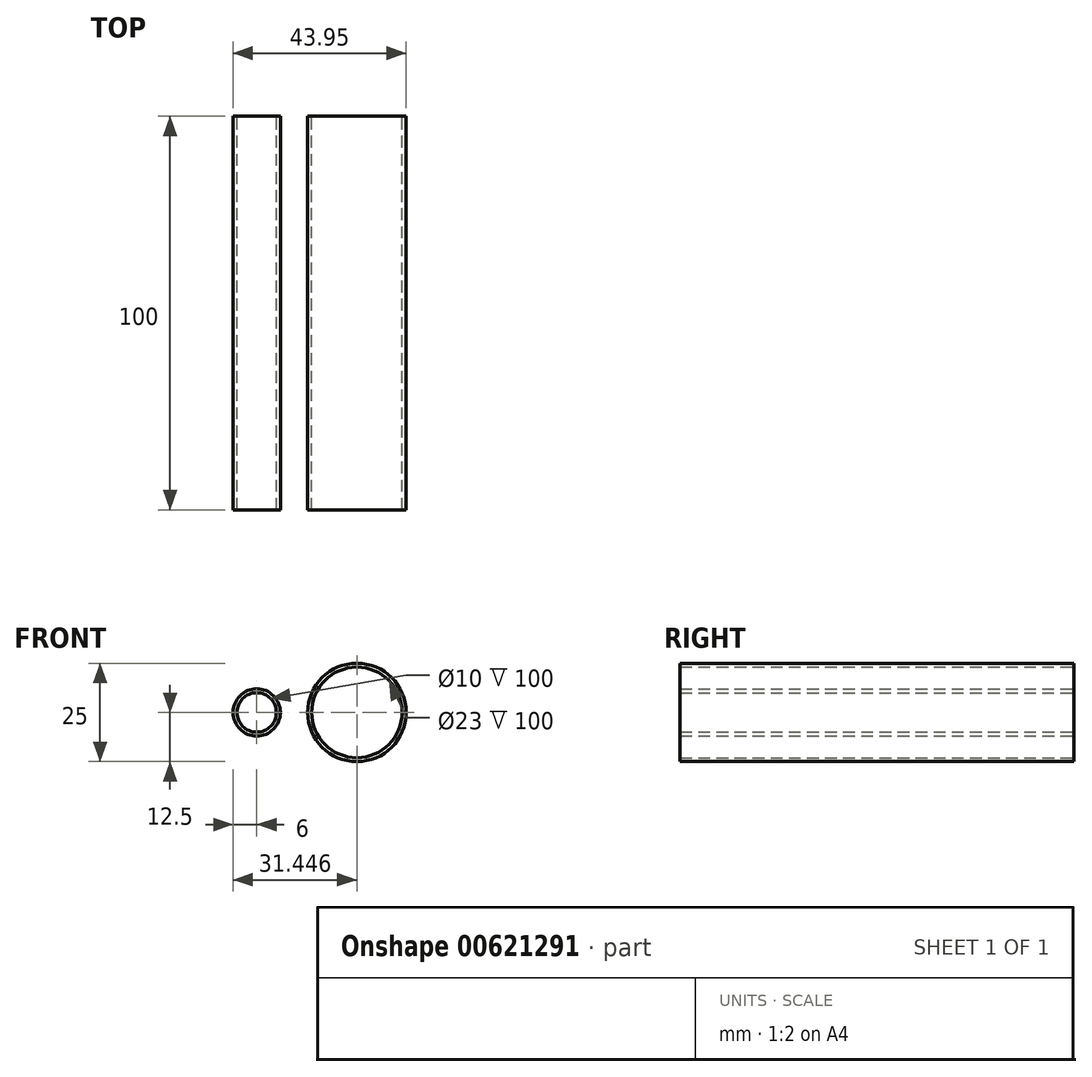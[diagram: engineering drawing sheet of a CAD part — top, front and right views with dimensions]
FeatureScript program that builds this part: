
annotation { "Feature Type Name" : "Feature", "Feature Type Description" : "" }
export const myFeature = defineFeature(function(context is Context, id is Id, definition is map)
    precondition{}
    {
        {
            var Q0;
            Q0=qCreatedBy(makeId("Front.planeOp"),FACE);
            var sketch = newSketch(context, id + "F0", { "sketchPlane" : qUnion([Q0])});
            skCircle(sketch, "E0", {"center": v(0, 0) * mm, "radius": 6 * mm});
            skCircle(sketch, "E1", {"center": v(0, 0) * mm, "radius": 5 * mm});
            skCircle(sketch, "E2", {"center": v(25.45, 0) * mm, "radius": 11.5 * mm});
            skCircle(sketch, "E3", {"center": v(25.45, 0) * mm, "radius": 12.5 * mm});
            skSolve(sketch);
        }
        {
            var Q0;
            Q0 = qSketchRegion(id + "F0", true);
            extrude(context, id + "F1", {"entities" : qUnion([Q0]), "endBound" : BoundingType.SYMMETRIC, "depth" : 100 * mm, "offsetDistance" : 25 * mm});
        }
    });
